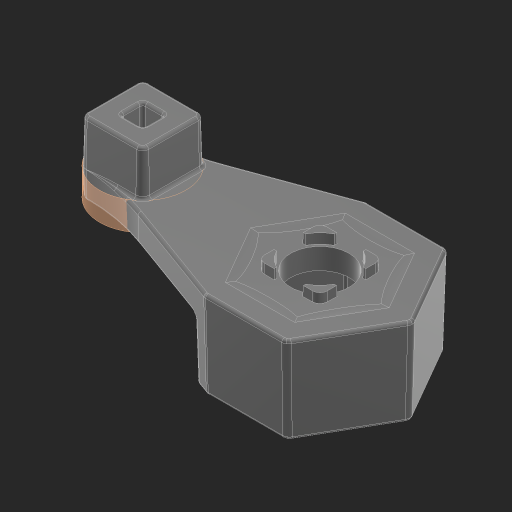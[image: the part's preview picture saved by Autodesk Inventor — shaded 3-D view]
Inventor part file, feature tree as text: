
AUTODESK INVENTOR PART (.ipt)
format: ipt  version: 2023 (Build 270158000, 158)  size: 624,128 bytes
history: native  units: in
note: dims shown in document units (in); Inventor stores cm internally (conversion verified against a paired STEP export)
features: sketch x1, other x1, fillet x1, extrude x1
ambient origin geometry x8: Origin, YZ Plane, XZ Plane, XY Plane, X Axis, Y Axis, Z Axis, Center Point
bodies: Solid1 (feature_tree)
feature tree (4):
  sketch  "Sketch1"
  other  "Srf1"
  fillet  "Fillet10"  Radius=0.0606in
  extrude  "ExtrusionSrf1"  [1 undecoded]
note: 1 required parameter value undecoded (feature->parameter linkage not recoverable at this tier; creation-order binding heuristic only, values carry confidence <= 0.55)
